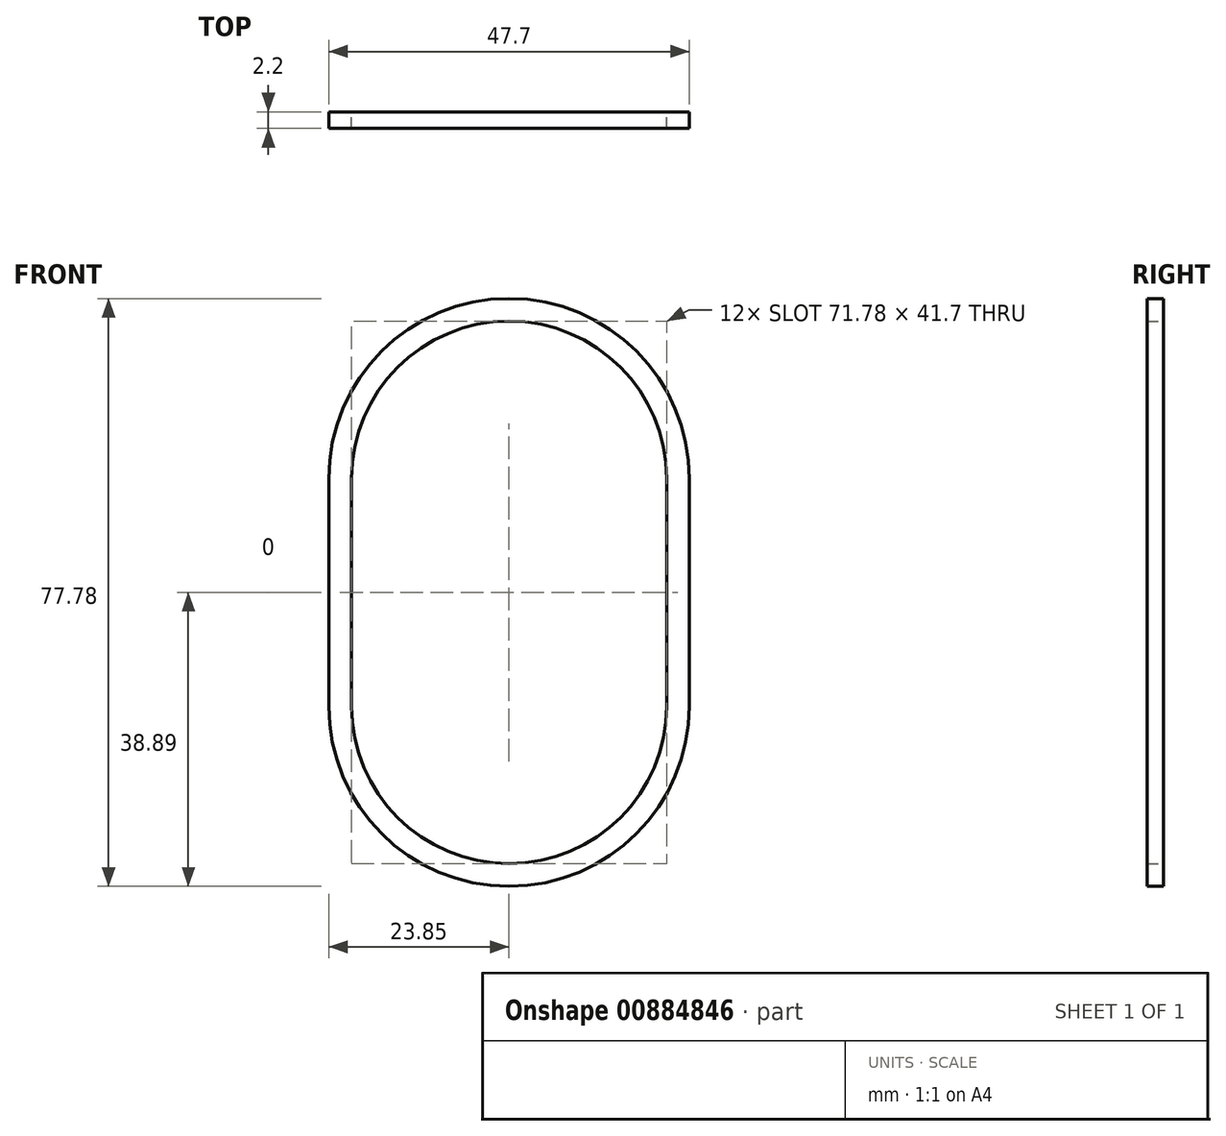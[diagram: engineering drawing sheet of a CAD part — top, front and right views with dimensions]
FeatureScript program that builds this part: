
annotation { "Feature Type Name" : "Feature", "Feature Type Description" : "" }
export const myFeature = defineFeature(function(context is Context, id is Id, definition is map)
    precondition{}
    {
        {
            var Q0;
            Q0=qCreatedBy(makeId("Front.planeOp"),FACE);
            var sketch = newSketch(context, id + "F0", { "sketchPlane" : qUnion([Q0])});
            skArc(sketch, "E0", {"start": v(23.85, 15.04) * mm, "mid": v(0, 38.9) * mm, "end": v(-23.85, 15.04) * mm});
            skArc(sketch, "E1.MirrorC", {"start": v(23.85, -15.04) * mm, "mid": v(0, -38.9) * mm, "end": v(-23.85, -15.04) * mm});
            skLineSegment(sketch, "E2", {"start": v(-23.85, 15.04) * mm, "end": v(-23.85, -15.04) * mm});
            skLineSegment(sketch, "E3.MirrorCS", {"start": v(23.85, 15.04) * mm, "end": v(23.85, -15.04) * mm});
            skSolve(sketch);
        }
        {
            var Q0;
            Q0=makeQuery(id+"F0.imprint","IMPRINT",FACE,{"disambiguationData":[TD([[makeQuery(id+"F0.imprint","IMPRINT",EDGE,{"derivedFrom":sQuery(id+"F0.wireOp",EDGE,"E0")}),1.0]])]});
            var sketch = newSketch(context, id + "F1", { "sketchPlane" : qUnion([Q0])});
            skLineSegment(sketch, "E4.0", {"start": v(23.85, -15.04) * mm, "end": v(23.85, 15.04) * mm});
            skArc(sketch, "E4.1", {"start": v(-23.85, -15.04) * mm, "mid": v(0, -38.9) * mm, "end": v(23.85, -15.04) * mm});
            skLineSegment(sketch, "E4.2", {"start": v(-23.85, 15.04) * mm, "end": v(-23.85, -15.04) * mm});
            skArc(sketch, "E5.0", {"start": v(-20.85, -15.04) * mm, "mid": v(0, -35.9) * mm, "end": v(20.85, -15.04) * mm});
            skLineSegment(sketch, "E5.1", {"start": v(-20.85, 15.04) * mm, "end": v(-20.85, -15.04) * mm});
            skArc(sketch, "E5.2", {"start": v(20.85, 15.04) * mm, "mid": v(0, 35.9) * mm, "end": v(-20.85, 15.04) * mm});
            skLineSegment(sketch, "E5.3", {"start": v(20.85, -15.04) * mm, "end": v(20.85, 15.04) * mm});
            skSolve(sketch);
        }
        {
            var Q0;
            Q0=makeQuery(id+"F1.imprint","IMPRINT",FACE,{"disambiguationData":[TD([[makeQuery(id+"F1.imprint","IMPRINT",EDGE,{"derivedFrom":sQuery(id+"F1.wireOp",EDGE,"E4.0")}),-1.0]])]});
            extrude(context, id + "F2", {"entities" : qUnion([Q0]), "depth" : 2.2 * mm, "offsetDistance" : 25 * mm});
        }
    });
